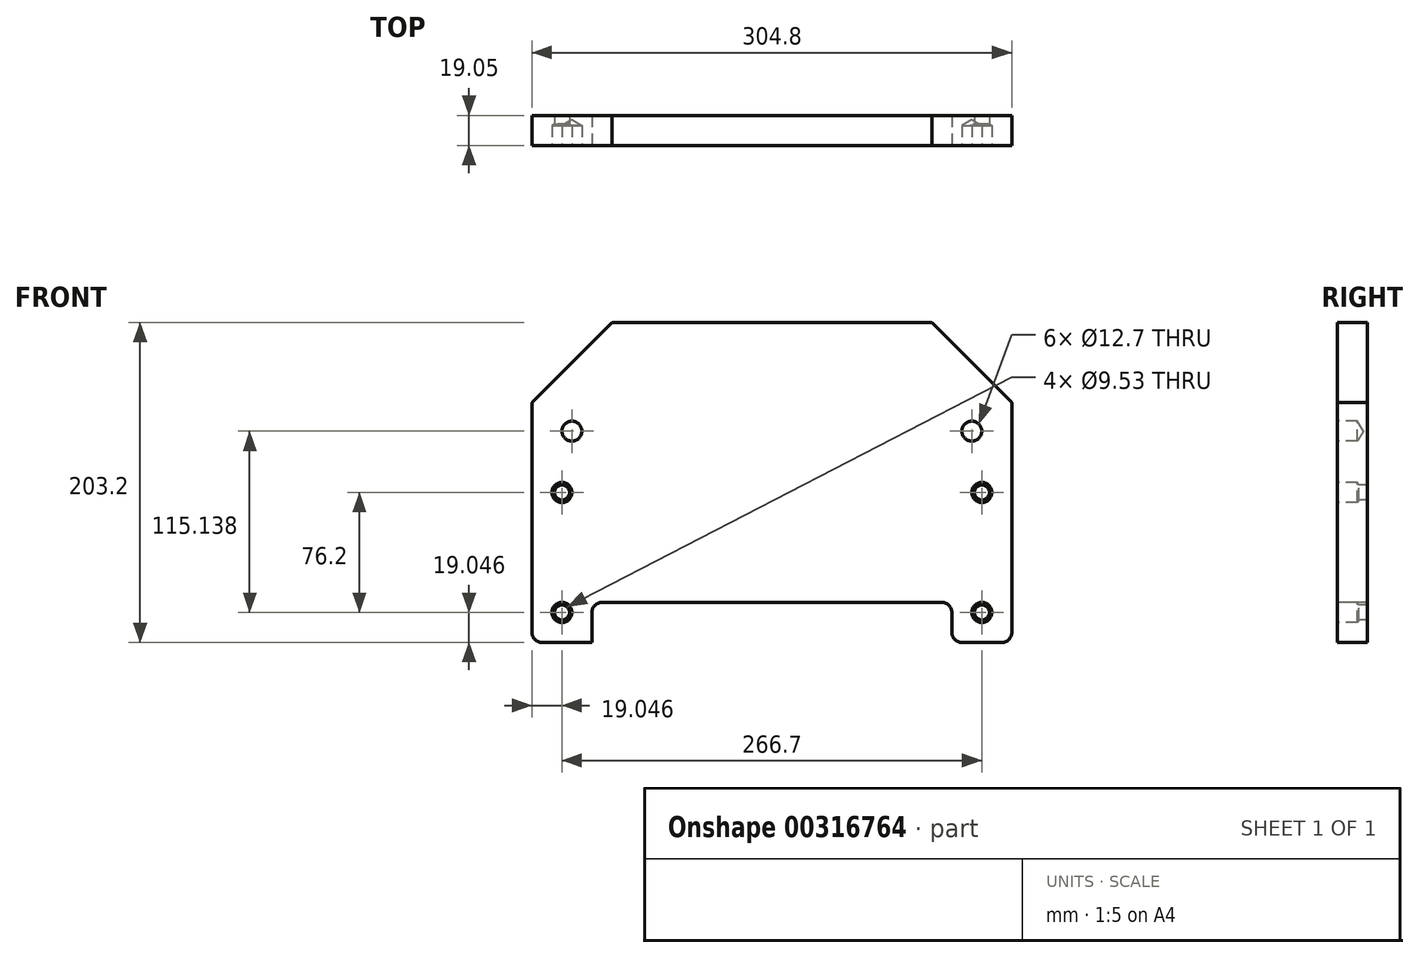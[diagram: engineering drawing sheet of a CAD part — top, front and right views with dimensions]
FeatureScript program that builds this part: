
annotation { "Feature Type Name" : "Feature", "Feature Type Description" : "" }
export const myFeature = defineFeature(function(context is Context, id is Id, definition is map)
    precondition{}
    {
        {
            var Q0;
            Q0=qCreatedBy(makeId("Front.planeOp"),FACE);
            var sketch = newSketch(context, id + "F0", { "sketchPlane" : qUnion([Q0])});
            skLineSegment(sketch, "E0.bottom", {"start": v(-13.14, 178.82) * mm, "end": v(291.66, 178.82) * mm});
            skLineSegment(sketch, "E0.top", {"start": v(-13.14, -24.38) * mm, "end": v(291.66, -24.38) * mm});
            skLineSegment(sketch, "E0.left", {"start": v(-13.14, 178.82) * mm, "end": v(-13.14, -24.38) * mm});
            skLineSegment(sketch, "E0.right", {"start": v(291.66, 178.82) * mm, "end": v(291.66, -24.38) * mm});
            skSolve(sketch);
        }
        {
            var Q0;
            Q0=makeQuery(id+"F0.imprint","IMPRINT",FACE,{"disambiguationData":[TD([[makeQuery(id+"F0.imprint","IMPRINT",EDGE,{"derivedFrom":sQuery(id+"F0.wireOp",EDGE,"E0.bottom")}),-1.0]])]});
            extrude(context, id + "F1", {"entities" : qUnion([Q0]), "depth" : 19.05 * mm});
        }
        {
            var Q0;
            Q0=makeQuery(id+"F1.opExtrude","SWEPT_EDGE",EDGE,{"disambiguationData":[OSD([sQuery(id+"F0.wireOp",EDGE,"E0.bottom"),sQuery(id+"F0.wireOp",EDGE,"E0.left")])]});
            var Q1;
            Q1=makeQuery(id+"F1.opExtrude","SWEPT_EDGE",EDGE,{"disambiguationData":[OSD([sQuery(id+"F0.wireOp",EDGE,"E0.bottom"),sQuery(id+"F0.wireOp",EDGE,"E0.right")])]});
            chamfer(context, id + "F2", {"entities" : qUnion([Q0, Q1]), "width" : 50.8 * mm, "tangentPropagation" : true});
        }
        {
            var Q0;
            Q0=makeQuery(id+"F1.opExtrude","CAP_FACE",FACE,{"disambiguationData":[OSD([sQuery(id+"F0.wireOp",EDGE,"E0.bottom"),sQuery(id+"F0.wireOp",EDGE,"E0.top"),sQuery(id+"F0.wireOp",EDGE,"E0.left"),sQuery(id+"F0.wireOp",EDGE,"E0.right")])],"isStart":false});
            var sketch = newSketch(context, id + "F3", { "sketchPlane" : qUnion([Q0])});
            skLineSegment(sketch, "E1.bottom", {"start": v(24.96, -24.38) * mm, "end": v(253.56, -24.38) * mm});
            skLineSegment(sketch, "E1.top", {"start": v(24.96, 1.02) * mm, "end": v(253.56, 1.02) * mm});
            skLineSegment(sketch, "E1.left", {"start": v(24.96, -24.38) * mm, "end": v(24.96, 1.02) * mm});
            skLineSegment(sketch, "E1.right", {"start": v(253.56, -24.38) * mm, "end": v(253.56, 1.02) * mm});
            skSolve(sketch);
        }
        {
            var Q0;
            Q0=makeQuery(id+"F3.imprint","IMPRINT",FACE,{"disambiguationData":[TD([[makeQuery(id+"F3.imprint","IMPRINT",EDGE,{"derivedFrom":sQuery(id+"F3.wireOp",EDGE,"E1.bottom")}),1.0]])]});
            extrude(context, id + "F4", {"entities" : qUnion([Q0]), "operationType" : NewBodyOperationType.REMOVE, "oppositeDirection" : true, "depth" : 19.05 * mm});
        }
        {
            var Q0;
            Q0=makeQuery(id+"F4.boolean.opBoolean","COPY",EDGE,{"derivedFrom":makeQuery(id+"F4.opExtrude","SWEPT_EDGE",EDGE,{"disambiguationData":[OSD([sQuery(id+"F3.wireOp",EDGE,"E1.top"),sQuery(id+"F3.wireOp",EDGE,"E1.left")])]})});
            var Q1;
            Q1=makeQuery(id+"F4.boolean.opBoolean","COPY",EDGE,{"derivedFrom":makeQuery(id+"F4.opExtrude","SWEPT_EDGE",EDGE,{"disambiguationData":[OSD([sQuery(id+"F3.wireOp",EDGE,"E1.top"),sQuery(id+"F3.wireOp",EDGE,"E1.right")])]})});
            var Q2;
            Q2=makeQuery(id+"F4.boolean.opBoolean","COPY",EDGE,{"derivedFrom":makeQuery(id+"F4.opExtrude","SWEPT_EDGE",EDGE,{"disambiguationData":[OSD([sQuery(id+"F0.wireOp",EDGE,"E0.top"),sQuery(id+"F3.wireOp",EDGE,"E1.bottom"),sQuery(id+"F3.wireOp",EDGE,"E1.right")])]})});
            var Q3;
            Q3=makeQuery(id+"F1.opExtrude","SWEPT_EDGE",EDGE,{"disambiguationData":[OSD([sQuery(id+"F0.wireOp",EDGE,"E0.top"),sQuery(id+"F0.wireOp",EDGE,"E0.right")])]});
            var Q4;
            Q4=makeQuery(id+"F4.boolean.opBoolean","COPY",EDGE,{"derivedFrom":makeQuery(id+"F4.opExtrude","SWEPT_EDGE",EDGE,{"disambiguationData":[OSD([sQuery(id+"F0.wireOp",EDGE,"E0.top"),sQuery(id+"F3.wireOp",EDGE,"E1.bottom"),sQuery(id+"F3.wireOp",EDGE,"E1.left")])]})});
            var Q5;
            Q5=makeQuery(id+"F1.opExtrude","SWEPT_EDGE",EDGE,{"disambiguationData":[OSD([sQuery(id+"F0.wireOp",EDGE,"E0.top"),sQuery(id+"F0.wireOp",EDGE,"E0.left")])]});
            fillet(context, id + "F5", {"entities" : qUnion([Q0, Q1, Q2, Q3, Q4, Q5]), "radius" : 6.35 * mm, "tangentPropagation" : true, "allowEdgeOverflow" : false});
        }
        {
            var Q0;
            Q0=makeQuery(id+"F1.opExtrude","CAP_FACE",FACE,{"disambiguationData":[OSD([sQuery(id+"F0.wireOp",EDGE,"E0.bottom"),sQuery(id+"F0.wireOp",EDGE,"E0.top"),sQuery(id+"F0.wireOp",EDGE,"E0.left"),sQuery(id+"F0.wireOp",EDGE,"E0.right")])],"isStart":false});
            var sketch = newSketch(context, id + "F6", { "sketchPlane" : qUnion([Q0])});
            skPoint(sketch, "E2", {"position": v(5.9, -5.33) * mm});
            skPoint(sketch, "E3", {"position": v(272.6, -5.33) * mm});
            skPoint(sketch, "E4", {"position": v(5.9, 70.87) * mm});
            skPoint(sketch, "E5", {"position": v(12.26, 109.8) * mm});
            skPoint(sketch, "E6", {"position": v(266.26, 109.8) * mm});
            skPoint(sketch, "E7", {"position": v(272.6, 70.87) * mm});
            skSolve(sketch);
        }
        {
            var Q0;
            Q0=sQuery(id+"F6.wireOp",VERTEX,"E5");
            var Q1;
            Q1=sQuery(id+"F6.wireOp",VERTEX,"E6");
            var Q2;
            Q2=makeQuery(id+"F1.opExtrude","SWEPT_BODY",BODY,{"disambiguationData":[OSD([sQuery(id+"F0.wireOp",EDGE,"E0.bottom"),sQuery(id+"F0.wireOp",EDGE,"E0.top"),sQuery(id+"F0.wireOp",EDGE,"E0.left"),sQuery(id+"F0.wireOp",EDGE,"E0.right")])]});
            hole(context, id + "F7", {"style" : HoleStyle.SIMPLE, "endStyle" : HoleEndStyle.BLIND, "holeDiameter" : 12.7 * mm, "holeDepth" : 12.7 * mm, "tappedDepth" : 12.7 * mm, "tapClearance" : 3, "locations" : qUnion([Q0, Q1]), "scope" : qUnion([Q2])});
        }
        {
            var Q0;
            Q0=sQuery(id+"F6.wireOp",VERTEX,"E7");
            var Q1;
            Q1=sQuery(id+"F6.wireOp",VERTEX,"E4");
            var Q2;
            Q2=sQuery(id+"F6.wireOp",VERTEX,"E2");
            var Q3;
            Q3=sQuery(id+"F6.wireOp",VERTEX,"E3");
            var Q4;
            Q4=makeQuery(id+"F1.opExtrude","SWEPT_BODY",BODY,{"disambiguationData":[OSD([sQuery(id+"F0.wireOp",EDGE,"E0.bottom"),sQuery(id+"F0.wireOp",EDGE,"E0.top"),sQuery(id+"F0.wireOp",EDGE,"E0.left"),sQuery(id+"F0.wireOp",EDGE,"E0.right")])]});
            hole(context, id + "F8", {"style" : HoleStyle.SIMPLE, "endStyle" : HoleEndStyle.BLIND, "holeDiameter" : 12.7 * mm, "holeDepth" : 12.7 * mm, "tappedDepth" : 12.7 * mm, "tapClearance" : 3, "locations" : qUnion([Q0, Q1, Q2, Q3]), "scope" : qUnion([Q4])});
        }
        {
            var Q0;
            Q0=sQuery(id+"F6.wireOp",VERTEX,"E4");
            var Q1;
            Q1=sQuery(id+"F6.wireOp",VERTEX,"E7");
            var Q2;
            Q2=sQuery(id+"F6.wireOp",VERTEX,"E2");
            var Q3;
            Q3=sQuery(id+"F6.wireOp",VERTEX,"E3");
            var Q4;
            Q4=makeQuery(id+"F1.opExtrude","SWEPT_BODY",BODY,{"disambiguationData":[OSD([sQuery(id+"F0.wireOp",EDGE,"E0.bottom"),sQuery(id+"F0.wireOp",EDGE,"E0.top"),sQuery(id+"F0.wireOp",EDGE,"E0.left"),sQuery(id+"F0.wireOp",EDGE,"E0.right")])]});
            hole(context, id + "F9", {"style" : HoleStyle.SIMPLE, "endStyle" : HoleEndStyle.THROUGH, "holeDiameter" : 9.52 * mm, "tappedDepth" : 12.7 * mm, "tapClearance" : 3, "locations" : qUnion([Q0, Q1, Q2, Q3]), "scope" : qUnion([Q4])});
        }
    });
